# Revit family: Haworth_Patterns_FileEnclosureVertical
name_source: partatom
category: Furniture Systems
revit_build: Autodesk Revit 2018 (Build: 20170223_1515(x64)
units: mm (PartAtom-declared; Revit-internal decimal feet)

## family parameters
Always vertical = Yes
Cut with Voids When Loaded = No
OmniClass Number = 23.40.70.14.64.21
OmniClass Title = Systems Furniture
Part Type = Normal
Room Calculation Point = No
Round Connector Dimension = Use Diameter
Shared = No
Work Plane-Based = No

## types (1)
- 42h 22d
    Actual Depth = 22"
    Actual Height = 42 1/2"
    Actual Width = 3"
    Assembly Code = E2020200
    Bench Finish = Haworth _ Wood _ White Oak
    Depth = 22"
    Description = Haworth - Patterns File Enclosure - Vertical
    Height = 42 1/2"
    Manufacturer = Haworth
    Max. Depth = 42"
    Max. Height = 66 1/2"
    Max. Width = 3"
    Min. Depth = 22"
    Min. Height = 30 1/2"
    Min. Width = 3"
    Model = Haworth - Patterns File Enclosure - Vertical
    Revision Number = 2
    Size = Verify Final Dim. w/ Haworth
    Standard Depths = 22, 42 in.
    Standard Outside Height = 30.5, 42.5, 54.5, 66.5 in.
    Sustainability Info = http://www.haworth.com
    URL = https://www.haworth.com
    URL - Product = https://www.haworth.com
    Vertical Width = 3"
    Warranty = http://www.haworth.com

## geometry (parser evidence)
native form markers: Sweep x3
no freeform markers — native parametric forms only
